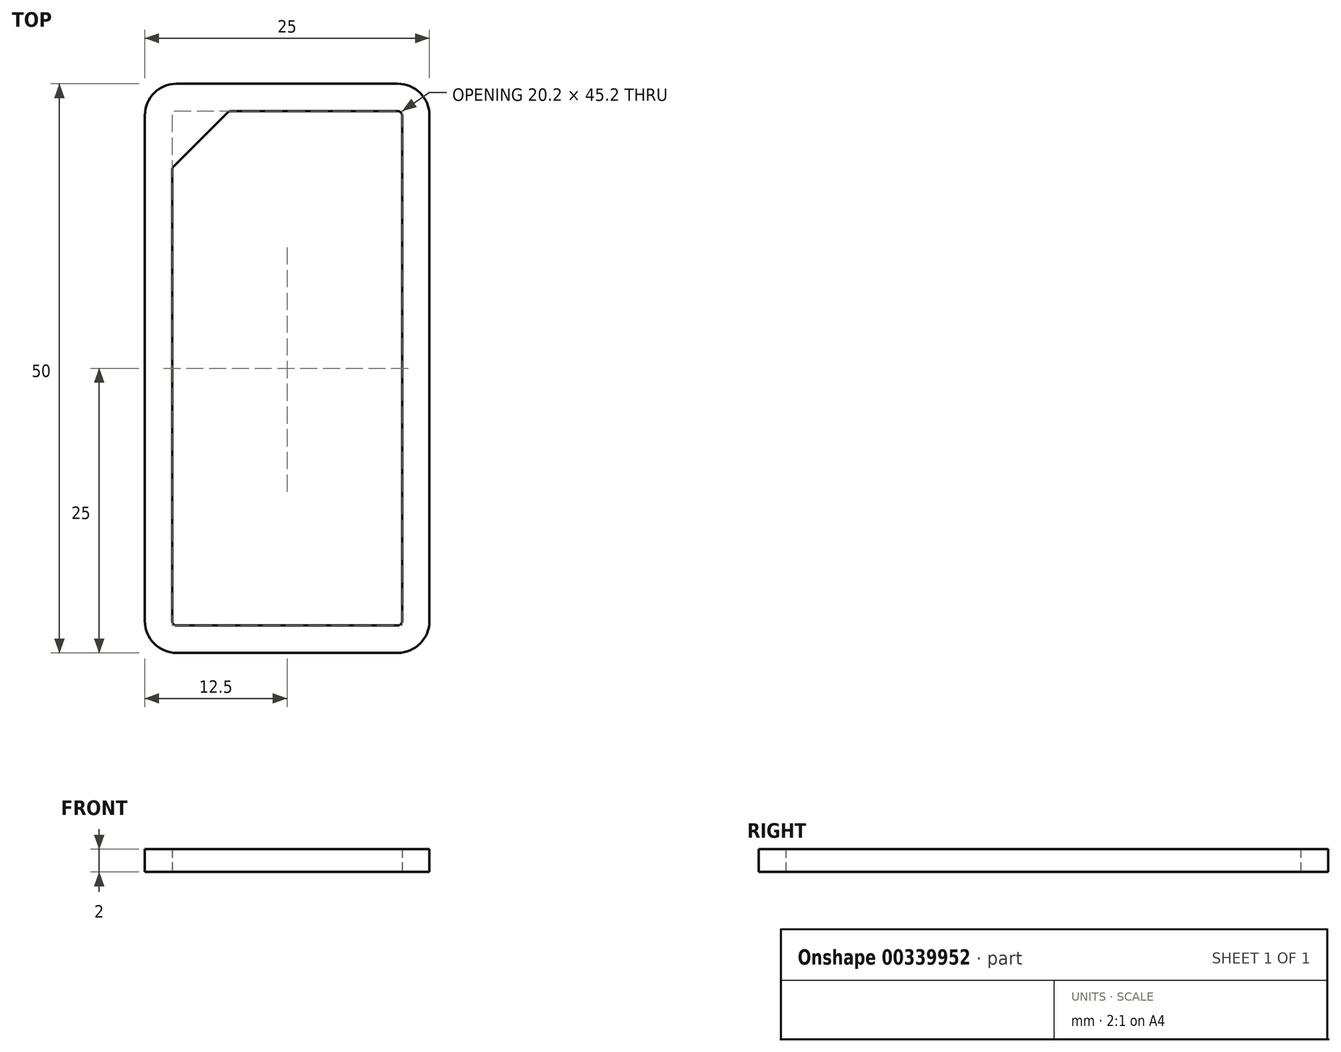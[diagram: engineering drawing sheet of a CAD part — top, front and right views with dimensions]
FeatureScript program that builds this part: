
annotation { "Feature Type Name" : "Feature", "Feature Type Description" : "" }
export const myFeature = defineFeature(function(context is Context, id is Id, definition is map)
    precondition{}
    {
        {
            var Q0;
            Q0=qCreatedBy(makeId("Top.planeOp"),FACE);
            var sketch = newSketch(context, id + "F0", { "sketchPlane" : qUnion([Q0])});
            skLineSegment(sketch, "E0.bottom", {"start": v(12.5, -25) * mm, "end": v(-12.5, -25) * mm});
            skLineSegment(sketch, "E0.top", {"start": v(12.5, 25) * mm, "end": v(-12.5, 25) * mm});
            skLineSegment(sketch, "E0.left", {"start": v(12.5, -25) * mm, "end": v(12.5, 25) * mm});
            skLineSegment(sketch, "E0.right", {"start": v(-12.5, -25) * mm, "end": v(-12.5, 25) * mm});
            skPoint(sketch, "E0.middle", {"position": v(0, 0) * mm});
            skLineSegment(sketch, "E1.bottom", {"start": v(-10.1, 22.6) * mm, "end": v(10.1, 22.6) * mm});
            skLineSegment(sketch, "E1.top", {"start": v(-10.1, -22.6) * mm, "end": v(10.1, -22.6) * mm});
            skLineSegment(sketch, "E1.left", {"start": v(-10.1, 22.6) * mm, "end": v(-10.1, -22.6) * mm});
            skLineSegment(sketch, "E1.right", {"start": v(10.1, 22.6) * mm, "end": v(10.1, -22.6) * mm});
            skLineSegment(sketch, "E2", {"start": v(-10.1, 17.6) * mm, "end": v(-5.1, 22.6) * mm});
            skSolve(sketch);
        }
        {
            var Q0;
            Q0 = qSketchRegion(id + "F0", true);
            var Q1;
            {var subQ3=sQuery(id+"F0.wireOp",EDGE,"E2");Q1=makeQuery(id+"F0.imprint","IMPRINT",FACE,{"disambiguationData":[TD([[makeQuery(id+"F0.imprint","IMPRINT",EDGE,{"derivedFrom":subQ3}),1.0]])]});}
            extrude(context, id + "F1", {"entities" : qUnion([Q0, Q1]), "depth" : 2 * mm});
        }
        {
            var Q0;
            Q0=makeQuery(id+"F1.opExtrude","SWEPT_EDGE",EDGE,{"disambiguationData":[OSD([sQuery(id+"F0.wireOp",EDGE,"E0.top"),sQuery(id+"F0.wireOp",EDGE,"E0.right")])]});
            var Q1;
            Q1=makeQuery(id+"F1.opExtrude","SWEPT_EDGE",EDGE,{"disambiguationData":[OSD([sQuery(id+"F0.wireOp",EDGE,"E0.bottom"),sQuery(id+"F0.wireOp",EDGE,"E0.right")])]});
            var Q2;
            Q2=makeQuery(id+"F1.opExtrude","SWEPT_EDGE",EDGE,{"disambiguationData":[OSD([sQuery(id+"F0.wireOp",EDGE,"E0.bottom"),sQuery(id+"F0.wireOp",EDGE,"E0.left")])]});
            var Q3;
            Q3=makeQuery(id+"F1.opExtrude","SWEPT_EDGE",EDGE,{"disambiguationData":[OSD([sQuery(id+"F0.wireOp",EDGE,"E0.top"),sQuery(id+"F0.wireOp",EDGE,"E0.left")])]});
            fillet(context, id + "F2", {"entities" : qUnion([Q0, Q1, Q2, Q3]), "radius" : 2.8 * mm, "tangentPropagation" : true, "allowEdgeOverflow" : false});
        }
        {
            var Q0;
            Q0=makeQuery(id+"F1.opExtrude","SWEPT_EDGE",EDGE,{"disambiguationData":[OSD([sQuery(id+"F0.wireOp",EDGE,"E1.bottom"),sQuery(id+"F0.wireOp",EDGE,"E1.right")])]});
            var Q1;
            Q1=makeQuery(id+"F1.opExtrude","SWEPT_EDGE",EDGE,{"disambiguationData":[OSD([sQuery(id+"F0.wireOp",EDGE,"E1.bottom"),sQuery(id+"F0.wireOp",EDGE,"E2")])]});
            var Q2;
            Q2=makeQuery(id+"F1.opExtrude","SWEPT_EDGE",EDGE,{"disambiguationData":[OSD([sQuery(id+"F0.wireOp",EDGE,"E1.left"),sQuery(id+"F0.wireOp",EDGE,"E2")])]});
            var Q3;
            Q3=makeQuery(id+"F1.opExtrude","SWEPT_EDGE",EDGE,{"disambiguationData":[OSD([sQuery(id+"F0.wireOp",EDGE,"E1.top"),sQuery(id+"F0.wireOp",EDGE,"E1.left")])]});
            var Q4;
            Q4=makeQuery(id+"F1.opExtrude","SWEPT_EDGE",EDGE,{"disambiguationData":[OSD([sQuery(id+"F0.wireOp",EDGE,"E1.top"),sQuery(id+"F0.wireOp",EDGE,"E1.right")])]});
            fillet(context, id + "F3", {"entities" : qUnion([Q0, Q1, Q2, Q3, Q4]), "radius" : 0.4 * mm, "tangentPropagation" : true, "allowEdgeOverflow" : false});
        }
    });
